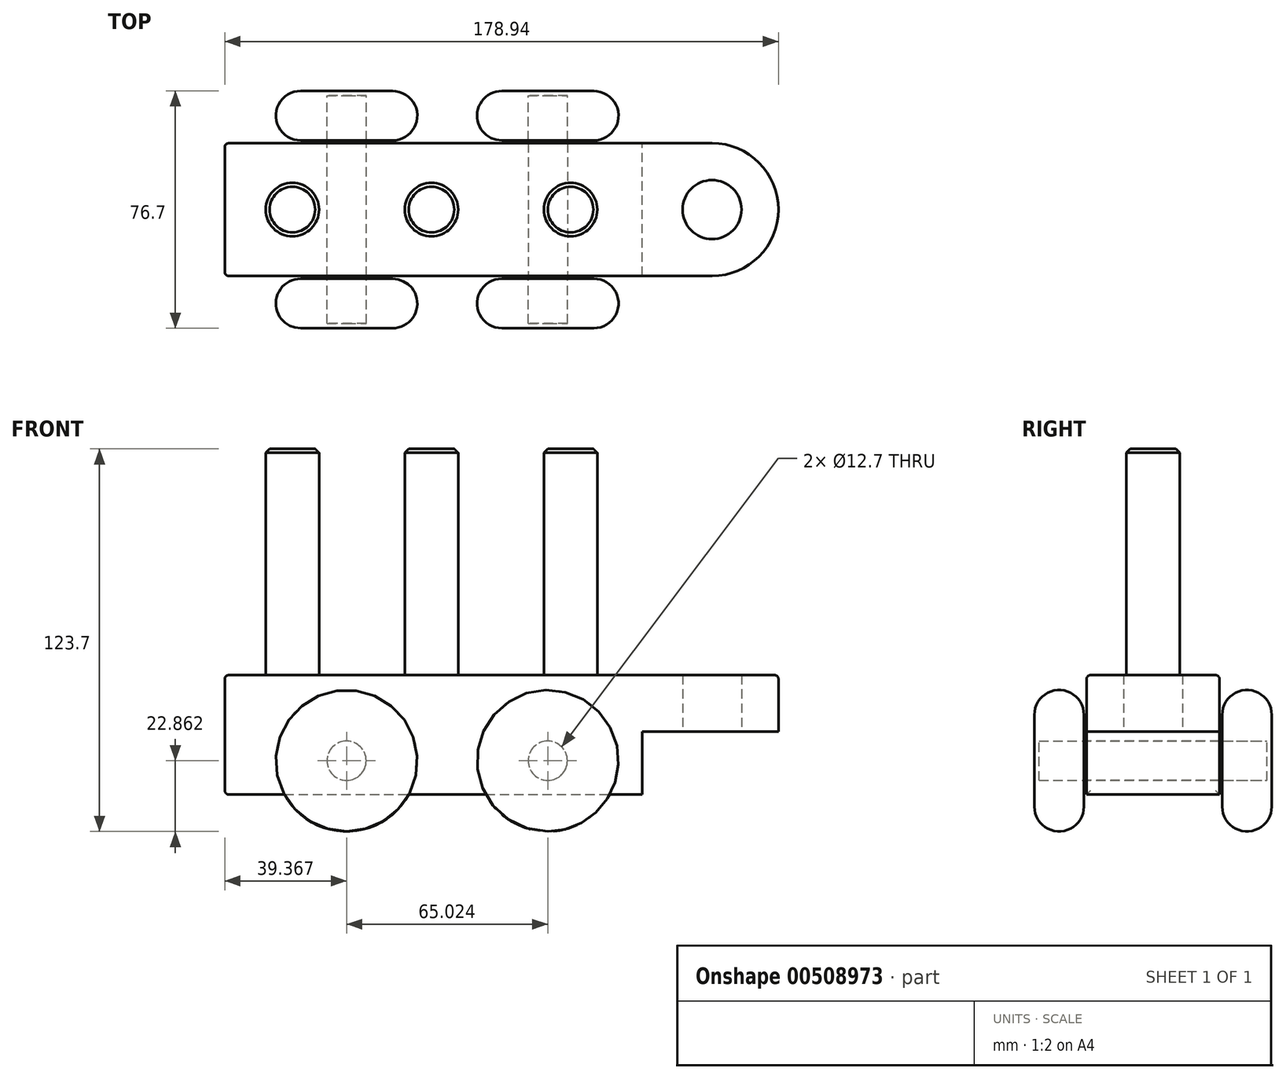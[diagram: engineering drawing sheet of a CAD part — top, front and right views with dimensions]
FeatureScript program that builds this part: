
annotation { "Feature Type Name" : "Feature", "Feature Type Description" : "" }
export const myFeature = defineFeature(function(context is Context, id is Id, definition is map)
    precondition{}
    {
        {
            var Q0;
            Q0=qCreatedBy(makeId("Top.planeOp"),FACE);
            var sketch = newSketch(context, id + "F0", { "sketchPlane" : qUnion([Q0])});
            skLineSegment(sketch, "E0.bottom", {"start": v(-178.94, 21.46) * mm, "end": v(-21.46, 21.46) * mm});
            skLineSegment(sketch, "E0.top", {"start": v(-178.94, -21.46) * mm, "end": v(-21.46, -21.46) * mm});
            skLineSegment(sketch, "E0.left", {"start": v(-178.94, 21.46) * mm, "end": v(-178.94, -21.46) * mm});
            skArc(sketch, "E1", {"start": v(-21.46, 21.46) * mm, "mid": v(0, 0) * mm, "end": v(-21.46, -21.46) * mm});
            skLineSegment(sketch, "E2", {"start": v(-21.46, 0) * mm, "end": v(0, 0) * mm, "construction": true});
            skCircle(sketch, "E3", {"center": v(-21.46, 0) * mm, "radius": 9.53 * mm});
            skSolve(sketch);
        }
        {
            var Q0;
            Q0 = qSketchRegion(id + "F0", true);
            extrude(context, id + "F1", {"entities" : qUnion([Q0]), "depth" : 38.6 * mm, "offsetDistance" : 25.4 * mm});
        }
        {
            var Q0;
            Q0=makeQuery(id+"F1.opExtrude","CAP_FACE",FACE,{"disambiguationData":[OSD([sQuery(id+"F0.wireOp",EDGE,"E0.bottom"),sQuery(id+"F0.wireOp",EDGE,"E0.top"),sQuery(id+"F0.wireOp",EDGE,"E0.left"),sQuery(id+"F0.wireOp",EDGE,"E1"),sQuery(id+"F0.wireOp",EDGE,"E3")])],"isStart":true});
            var sketch = newSketch(context, id + "F2", { "sketchPlane" : qUnion([Q0])});
            skLineSegment(sketch, "E4", {"start": v(-44.07, 21.46) * mm, "end": v(-44.07, -21.46) * mm});
            skSolve(sketch);
        }
        {
            var Q0;
            Q0 = qSketchRegion(id + "F2", true);
            var Q1;
            {var subQ2=sQuery(id+"F2.wireOp",EDGE,"E4");Q1=makeQuery(id+"F2.imprint","IMPRINT",FACE,{"disambiguationData":[TD([[makeQuery(id+"F2.imprint","IMPRINT",EDGE,{"derivedFrom":subQ2}),1.0]])]});}
            extrude(context, id + "F3", {"entities" : qUnion([Q0, Q1]), "operationType" : NewBodyOperationType.REMOVE, "oppositeDirection" : true, "depth" : 20.32 * mm, "offsetDistance" : 25.4 * mm});
        }
        {
            var Q0;
            Q0=makeQuery(id+"F1.opExtrude","SWEPT_FACE",FACE,{"disambiguationData":[OSD([sQuery(id+"F0.wireOp",EDGE,"E0.top")])]});
            var sketch = newSketch(context, id + "F4", { "sketchPlane" : qUnion([Q0])});
            skLineSegment(sketch, "E5.0", {"start": v(-178.94, 38.6) * mm, "end": v(-21.46, 38.6) * mm});
            skLineSegment(sketch, "E6.0", {"start": v(-44.07, 20.32) * mm, "end": v(-44.07, 0) * mm});
            skLineSegment(sketch, "E7.0", {"start": v(-178.94, 0) * mm, "end": v(-44.07, 0) * mm});
            skLineSegment(sketch, "E8.0", {"start": v(-178.94, 38.6) * mm, "end": v(-178.94, 0) * mm});
            skCircle(sketch, "E9", {"center": v(-139.57, 10.92) * mm, "radius": 6.35 * mm});
            skCircle(sketch, "E10", {"center": v(-74.55, 10.92) * mm, "radius": 6.35 * mm});
            skSolve(sketch);
        }
        {
            var Q0;
            Q0=makeQuery(id+"F4.imprint","IMPRINT",FACE,{"disambiguationData":[TD([[makeQuery(id+"F4.imprint","IMPRINT",EDGE,{"derivedFrom":sQuery(id+"F4.wireOp",EDGE,"E9")}),1.0]])]});
            var Q1;
            Q1=makeQuery(id+"F4.imprint","IMPRINT",FACE,{"disambiguationData":[TD([[makeQuery(id+"F4.imprint","IMPRINT",EDGE,{"derivedFrom":sQuery(id+"F4.wireOp",EDGE,"E10")}),1.0]])]});
            var Q2;
            Q2=makeQuery(id+"F1.opExtrude","SWEPT_FACE",FACE,{"disambiguationData":[OSD([sQuery(id+"F0.wireOp",EDGE,"E0.bottom")])]});
            extrude(context, id + "F5", {"entities" : qUnion([Q0, Q1]), "operationType" : NewBodyOperationType.REMOVE, "endBound" : BoundingType.UP_TO_SURFACE, "oppositeDirection" : true, "depth" : 25.4 * mm, "endBoundEntityFace" : qUnion([Q2]), "offsetDistance" : 25.4 * mm});
        }
        {
            var Q0;
            Q0=makeQuery(id+"F1.opExtrude","CAP_FACE",FACE,{"disambiguationData":[OSD([sQuery(id+"F0.wireOp",EDGE,"E0.bottom"),sQuery(id+"F0.wireOp",EDGE,"E0.top"),sQuery(id+"F0.wireOp",EDGE,"E0.left"),sQuery(id+"F0.wireOp",EDGE,"E1"),sQuery(id+"F0.wireOp",EDGE,"E3")])],"isStart":false});
            var sketch = newSketch(context, id + "F6", { "sketchPlane" : qUnion([Q0])});
            skCircle(sketch, "E11", {"center": v(-157.1, 0) * mm, "radius": 8.64 * mm});
            skCircle(sketch, "E12", {"center": v(-112.14, 0) * mm, "radius": 8.64 * mm});
            skCircle(sketch, "E13", {"center": v(-67.18, 0) * mm, "radius": 8.64 * mm});
            skSolve(sketch);
        }
        {
            var Q0;
            Q0 = qSketchRegion(id + "F6", true);
            extrude(context, id + "F7", {"entities" : qUnion([Q0]), "operationType" : NewBodyOperationType.ADD, "depth" : 73.15 * mm, "offsetDistance" : 25.4 * mm});
        }
        {
            var Q0;
            Q0=makeQuery(id+"F7.opExtrude","CAP_EDGE",EDGE,{"disambiguationData":[OSD([sQuery(id+"F6.wireOp",EDGE,"E11")])],"isStart":false});
            var Q1;
            Q1=makeQuery(id+"F7.opExtrude","CAP_EDGE",EDGE,{"disambiguationData":[OSD([sQuery(id+"F6.wireOp",EDGE,"E12")])],"isStart":false});
            var Q2;
            Q2=makeQuery(id+"F7.opExtrude","CAP_EDGE",EDGE,{"disambiguationData":[OSD([sQuery(id+"F6.wireOp",EDGE,"E13")])],"isStart":false});
            chamfer(context, id + "F8", {"entities" : qUnion([Q0, Q1, Q2]), "width" : 1.27 * mm, "tangentPropagation" : true});
        }
        {
            var Q0;
            Q0=makeQuery(id+"F1.opExtrude","CAP_EDGE",EDGE,{"disambiguationData":[OSD([sQuery(id+"F0.wireOp",EDGE,"E0.bottom")])],"isStart":false});
            var Q1;
            Q1=makeQuery(id+"F1.opExtrude","CAP_EDGE",EDGE,{"disambiguationData":[OSD([sQuery(id+"F0.wireOp",EDGE,"E1")])],"isStart":false});
            var Q2;
            Q2=makeQuery(id+"F1.opExtrude","CAP_EDGE",EDGE,{"disambiguationData":[OSD([sQuery(id+"F0.wireOp",EDGE,"E0.top")])],"isStart":false});
            var Q3;
            Q3=makeQuery(id+"F1.opExtrude","CAP_EDGE",EDGE,{"disambiguationData":[OSD([sQuery(id+"F0.wireOp",EDGE,"E0.left")])],"isStart":false});
            var Q4;
            Q4=makeQuery(id+"F1.opExtrude","SWEPT_EDGE",EDGE,{"disambiguationData":[OSD([sQuery(id+"F0.wireOp",EDGE,"E0.bottom"),sQuery(id+"F0.wireOp",EDGE,"E0.left")])]});
            var Q5;
            Q5=makeQuery(id+"F1.opExtrude","CAP_EDGE",EDGE,{"disambiguationData":[OSD([sQuery(id+"F0.wireOp",EDGE,"E0.left")])],"isStart":true});
            var Q6;
            Q6=makeQuery(id+"F1.opExtrude","SWEPT_EDGE",EDGE,{"disambiguationData":[OSD([sQuery(id+"F0.wireOp",EDGE,"E0.top"),sQuery(id+"F0.wireOp",EDGE,"E0.left")])]});
            fillet(context, id + "F9", {"entities" : qUnion([Q0, Q1, Q2, Q3, Q4, Q5, Q6]), "radius" : 1.27 * mm, "tangentPropagation" : true, "allowEdgeOverflow" : false});
        }
        {
            var Q0;
            Q0=qCreatedBy(makeId("Front.planeOp"),FACE);
            var sketch = newSketch(context, id + "F10", { "sketchPlane" : qUnion([Q0])});
            skCircle(sketch, "E14.0", {"center": v(-139.57, 10.92) * mm, "radius": 6.35 * mm});
            skCircle(sketch, "E15.0", {"center": v(-74.55, 10.92) * mm, "radius": 6.35 * mm});
            skSolve(sketch);
        }
        {
            var Q0;
            Q0 = qSketchRegion(id + "F10", true);
            extrude(context, id + "F11", {"entities" : qUnion([Q0]), "endBound" : BoundingType.SYMMETRIC, "depth" : 73.66 * mm, "offsetDistance" : 25.4 * mm});
        }
        {
            var Q0;
            Q0=makeQuery(id+"F11.opExtrude","CAP_FACE",FACE,{"disambiguationData":[OSD([sQuery(id+"F10.wireOp",EDGE,"E14.0")])],"isStart":false});
            var sketch = newSketch(context, id + "F12", { "sketchPlane" : qUnion([Q0])});
            skCircle(sketch, "E16", {"center": v(-139.57, 10.92) * mm, "radius": 22.86 * mm});
            skCircle(sketch, "E17.0.0", {"center": v(-74.55, 10.92) * mm, "radius": 6.35 * mm});
            skCircle(sketch, "E18", {"center": v(-74.55, 10.92) * mm, "radius": 22.86 * mm});
            skSolve(sketch);
        }
        {
            var Q0;
            Q0 = qSketchRegion(id + "F12", true);
            var Q1;
            Q1=makeQuery(id+"F12.imprint","IMPRINT",FACE,{"disambiguationData":[TD([[makeQuery(id+"F12.imprint","IMPRINT",EDGE,{"derivedFrom":sQuery(id+"F12.wireOp",EDGE,"E17.0.0")}),1.0]])]});
            extrude(context, id + "F13", {"entities" : qUnion([Q0, Q1]), "depth" : 1.52 * mm, "offsetDistance" : 25.4 * mm, "hasSecondDirection" : true, "secondDirectionOppositeDirection" : true, "secondDirectionDepth" : 14.48 * mm});
        }
        {
            var Q0;
            Q0=makeQuery(id+"F11.opExtrude","CAP_FACE",FACE,{"disambiguationData":[OSD([sQuery(id+"F10.wireOp",EDGE,"E15.0")])],"isStart":true});
            var sketch = newSketch(context, id + "F14", { "sketchPlane" : qUnion([Q0])});
            skCircle(sketch, "E19.0", {"center": v(139.57, 10.92) * mm, "radius": 6.35 * mm});
            skCircle(sketch, "E20.0", {"center": v(74.55, 10.92) * mm, "radius": 6.35 * mm});
            skCircle(sketch, "E21", {"center": v(74.55, 10.92) * mm, "radius": 22.86 * mm});
            skCircle(sketch, "E22", {"center": v(139.57, 10.92) * mm, "radius": 22.86 * mm});
            skSolve(sketch);
        }
        {
            var Q0;
            Q0 = qSketchRegion(id + "F14", true);
            var Q1;
            Q1=makeQuery(id+"F14.imprint","IMPRINT",FACE,{"disambiguationData":[TD([[makeQuery(id+"F14.imprint","IMPRINT",EDGE,{"derivedFrom":sQuery(id+"F14.wireOp",EDGE,"E20.0")}),-1.0]])]});
            var Q2;
            Q2=makeQuery(id+"F14.imprint","IMPRINT",FACE,{"disambiguationData":[TD([[makeQuery(id+"F14.imprint","IMPRINT",EDGE,{"derivedFrom":sQuery(id+"F14.wireOp",EDGE,"E19.0")}),1.0]])]});
            extrude(context, id + "F15", {"entities" : qUnion([Q0, Q1, Q2]), "depth" : 1.52 * mm, "offsetDistance" : 25.4 * mm, "hasSecondDirection" : true, "secondDirectionOppositeDirection" : true, "secondDirectionDepth" : 14.48 * mm});
        }
        {
            var Q0;
            Q0=makeQuery(id+"F13.opExtrude","CAP_EDGE",EDGE,{"disambiguationData":[OSD([sQuery(id+"F12.wireOp",EDGE,"E18")])],"isStart":false});
            var Q1;
            Q1=makeQuery(id+"F13.opExtrude","CAP_EDGE",EDGE,{"disambiguationData":[OSD([sQuery(id+"F12.wireOp",EDGE,"E16")])],"isStart":false});
            var Q2;
            Q2=makeQuery(id+"F13.opExtrude","CAP_EDGE",EDGE,{"disambiguationData":[OSD([sQuery(id+"F12.wireOp",EDGE,"E16")])],"isStart":true});
            var Q3;
            Q3=makeQuery(id+"F15.opExtrude","CAP_EDGE",EDGE,{"disambiguationData":[OSD([sQuery(id+"F14.wireOp",EDGE,"E22")])],"isStart":false});
            var Q4;
            Q4=makeQuery(id+"F15.opExtrude","CAP_EDGE",EDGE,{"disambiguationData":[OSD([sQuery(id+"F14.wireOp",EDGE,"E22")])],"isStart":true});
            var Q5;
            Q5=makeQuery(id+"F15.opExtrude","CAP_EDGE",EDGE,{"disambiguationData":[OSD([sQuery(id+"F14.wireOp",EDGE,"E21")])],"isStart":true});
            var Q6;
            Q6=makeQuery(id+"F15.opExtrude","CAP_EDGE",EDGE,{"disambiguationData":[OSD([sQuery(id+"F14.wireOp",EDGE,"E21")])],"isStart":false});
            var Q7;
            Q7=makeQuery(id+"F13.opExtrude","CAP_EDGE",EDGE,{"disambiguationData":[OSD([sQuery(id+"F12.wireOp",EDGE,"E18")])],"isStart":true});
            fillet(context, id + "F16", {"entities" : qUnion([Q0, Q1, Q2, Q3, Q4, Q5, Q6, Q7]), "radius" : 8 * mm, "tangentPropagation" : true, "allowEdgeOverflow" : false});
        }
    });
